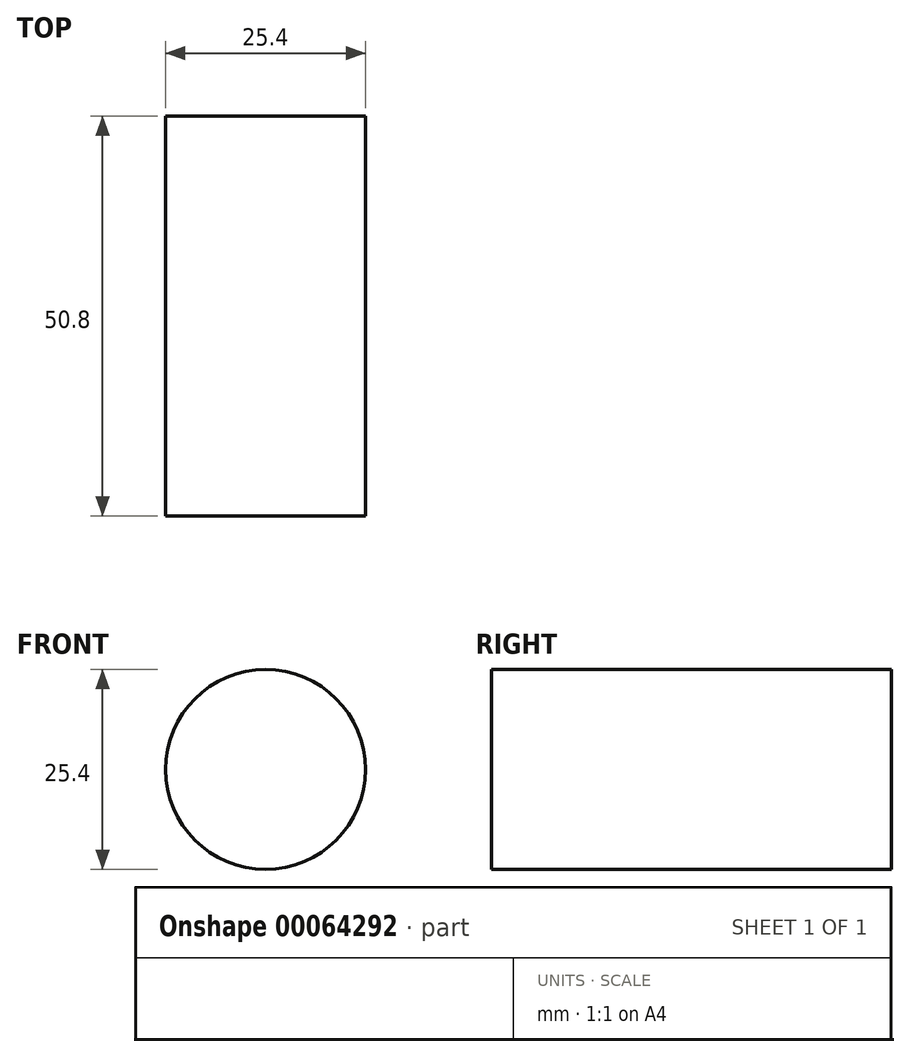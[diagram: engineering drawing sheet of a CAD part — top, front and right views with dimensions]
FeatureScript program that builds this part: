
annotation { "Feature Type Name" : "Feature", "Feature Type Description" : "" }
export const myFeature = defineFeature(function(context is Context, id is Id, definition is map)
    precondition{}
    {
        {
            var Q0;
            Q0=qCreatedBy(makeId("Front.planeOp"),FACE);
            var sketch = newSketch(context, id + "F0", { "sketchPlane" : qUnion([Q0])});
            skCircle(sketch, "E0", {"center": v(0, -1.42) * mm, "radius": 12.7 * mm});
            skSolve(sketch);
        }
        {
            var Q0;
            Q0=makeQuery(id+"F0.imprint","IMPRINT",FACE,{"disambiguationData":[TD([[makeQuery(id+"F0.imprint","IMPRINT",EDGE,{"derivedFrom":sQuery(id+"F0.wireOp",EDGE,"E0")}),1.0]])]});
            extrude(context, id + "F1", {"entities" : qUnion([Q0]), "depth" : 50.8 * mm});
        }
    });
